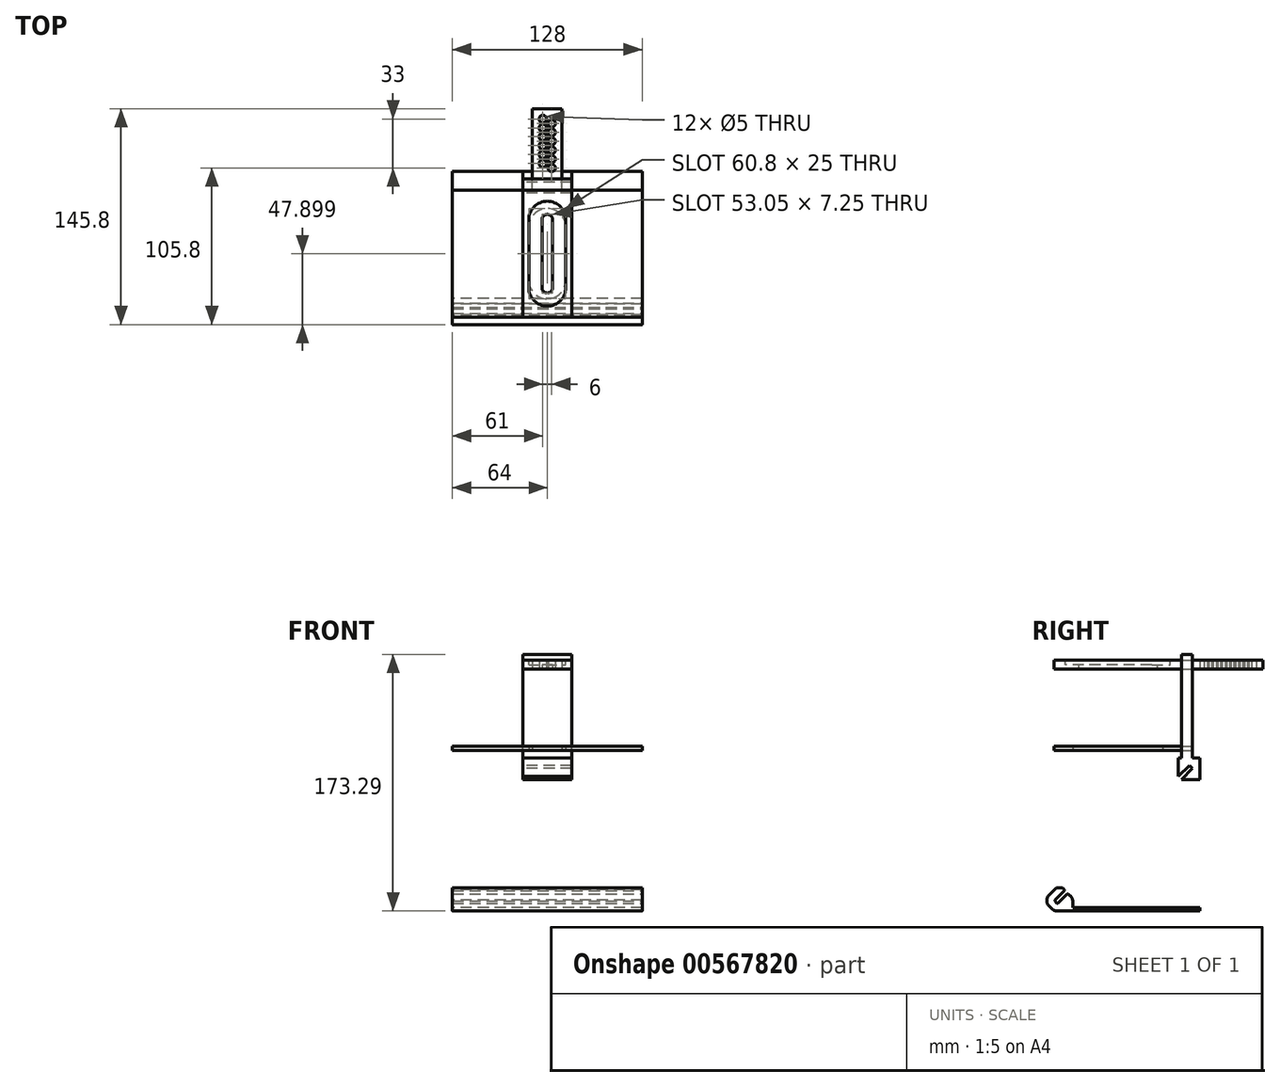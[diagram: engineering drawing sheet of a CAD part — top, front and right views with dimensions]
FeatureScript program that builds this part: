
annotation { "Feature Type Name" : "Feature", "Feature Type Description" : "" }
export const myFeature = defineFeature(function(context is Context, id is Id, definition is map)
    precondition{}
    {
        {
            assignVariable(context, id + "F0", {"name" : "spgBreite", "anyValue" : 128 * mm});
        }
        {
            assignVariable(context, id + "F1", {"name" : "abstDuesen", "anyValue" : 33 * mm});
        }
        {
            var Q0;
            Q0=qCreatedBy(makeId("Right.planeOp"),FACE);
            var sketch = newSketch(context, id + "F2", { "sketchPlane" : qUnion([Q0])});
            skLineSegment(sketch, "E0", {"start": v(0, 0) * mm, "end": v(0, 65) * mm, "construction": true});
            skLineSegment(sketch, "E1", {"start": v(0, 65) * mm, "end": v(-3.25, 65) * mm, "construction": true});
            skLineSegment(sketch, "E2", {"start": v(-3.25, 65) * mm, "end": v(-3.25, 81) * mm, "construction": true});
            skLineSegment(sketch, "E3", {"start": v(-3.25, 81) * mm, "end": v(14.75, 81) * mm, "construction": true});
            skLineSegment(sketch, "E4", {"start": v(14.75, 81) * mm, "end": v(14.75, 0) * mm, "construction": true});
            skLineSegment(sketch, "E5", {"start": v(14.75, 0) * mm, "end": v(0, 0) * mm, "construction": true});
            skLineSegment(sketch, "E6", {"start": v(0, 0) * mm, "end": v(-5, 0) * mm, "construction": true});
            skLineSegment(sketch, "E7", {"start": v(-5, 0) * mm, "end": v(-5, 20) * mm, "construction": true});
            skLineSegment(sketch, "E8", {"start": v(-5, 20) * mm, "end": v(-7.09, 22.09) * mm, "construction": true});
            skLineSegment(sketch, "E9", {"start": v(-7.09, 22.09) * mm, "end": v(-98.3, -69.13) * mm, "construction": true});
            skLineSegment(sketch, "E10", {"start": v(-98.3, -69.13) * mm, "end": v(-96.22, -71.22) * mm, "construction": true});
            skLineSegment(sketch, "E11", {"start": v(-96.22, -71.22) * mm, "end": v(-5, 20) * mm, "construction": true});
            skLineSegment(sketch, "E12", {"start": v(0, 0) * mm, "end": v(0, -150) * mm, "construction": true});
            skLineSegment(sketch, "E13", {"start": v(-98.3, -69.13) * mm, "end": v(-91.23, -62.06) * mm});
            skLineSegment(sketch, "E14", {"start": v(-91.23, -62.06) * mm, "end": v(-94.77, -58.52) * mm});
            skLineSegment(sketch, "E15", {"start": v(-94.77, -58.52) * mm, "end": v(-105.37, -69.13) * mm});
            skLineSegment(sketch, "E16", {"start": v(-105.37, -69.13) * mm, "end": v(-98.3, -76.2) * mm});
            skLineSegment(sketch, "E17", {"start": v(-98.3, -76.2) * mm, "end": v(0, -76.2) * mm});
            skLineSegment(sketch, "E18", {"start": v(0, -76.2) * mm, "end": v(0, -73.7) * mm});
            skLineSegment(sketch, "E19", {"start": v(-85.61, -67.68) * mm, "end": v(-89.15, -64.15) * mm});
            skLineSegment(sketch, "E20", {"start": v(-89.15, -64.15) * mm, "end": v(-96.22, -71.22) * mm});
            skLineSegment(sketch, "E21", {"start": v(-98.3, -69.13) * mm, "end": v(-96.22, -71.22) * mm});
            skLineSegment(sketch, "E22", {"start": v(-85.61, -67.68) * mm, "end": v(-85.61, -73.7) * mm});
            skLineSegment(sketch, "E23", {"start": v(-85.61, -73.7) * mm, "end": v(0, -73.7) * mm});
            skLineSegment(sketch, "E24", {"start": v(-7.09, 22.09) * mm, "end": v(-14.59, 14.59) * mm});
            skLineSegment(sketch, "E25", {"start": v(-12.5, 27.09) * mm, "end": v(-12.5, 97.09) * mm});
            skLineSegment(sketch, "E26", {"start": v(-5, 97.09) * mm, "end": v(-5, 27.09) * mm});
            skLineSegment(sketch, "E27", {"start": v(-5, 27.09) * mm, "end": v(0, 27.09) * mm});
            skLineSegment(sketch, "E28", {"start": v(0, 27.09) * mm, "end": v(0, 12.5) * mm});
            skLineSegment(sketch, "E29", {"start": v(0, 12.5) * mm, "end": v(-12.5, 12.5) * mm});
            skLineSegment(sketch, "E30", {"start": v(-12.5, 12.5) * mm, "end": v(-5, 20) * mm});
            skLineSegment(sketch, "E31", {"start": v(-5, 20) * mm, "end": v(-7.09, 22.09) * mm});
            skLineSegment(sketch, "E32", {"start": v(-98.3, -69.13) * mm, "end": v(-98.3, 130.87) * mm, "construction": true});
            skLineSegment(sketch, "E33", {"start": v(-98.3, -69.13) * mm, "end": v(-98.3, -169.13) * mm, "construction": true});
            skLineSegment(sketch, "E34", {"start": v(-12.5, 27.09) * mm, "end": v(-5, 27.09) * mm, "construction": true});
            skLineSegment(sketch, "E35", {"start": v(-14.5, 27.09) * mm, "end": v(-12.5, 27.09) * mm});
            skLineSegment(sketch, "E36", {"start": v(-14.5, 27.09) * mm, "end": v(-14.59, 14.59) * mm});
            skLineSegment(sketch, "E37", {"start": v(-12.5, 97.09) * mm, "end": v(-5, 97.09) * mm});
            skSolve(sketch);
        }
        {
            var Q0;
            Q0=makeQuery(id+"F2.imprint","IMPRINT",FACE,{"disambiguationData":[TD([[makeQuery(id+"F2.imprint","IMPRINT",EDGE,{"derivedFrom":sQuery(id+"F2.wireOp",EDGE,"E13")}),1.0]])]});
            extrude(context, id + "F3", {"entities" : qUnion([Q0]), "endBound" : BoundingType.SYMMETRIC, "depth" : getVariable(context, 'spgBreite'), "offsetDistance" : 25 * mm});
        }
        {
            var Q0;
            Q0=makeQuery(id+"F3.opExtrude","SWEPT_EDGE",EDGE,{"disambiguationData":[OSD([sQuery(id+"F2.wireOp",EDGE,"E15"),sQuery(id+"F2.wireOp",EDGE,"E16")])]});
            var Q1;
            Q1=makeQuery(id+"F3.opExtrude","SWEPT_EDGE",EDGE,{"disambiguationData":[OSD([sQuery(id+"F2.wireOp",EDGE,"E16"),sQuery(id+"F2.wireOp",EDGE,"E17")])]});
            fillet(context, id + "F4", {"entities" : qUnion([Q0, Q1]), "radius" : 5 * mm, "tangentPropagation" : true, "allowEdgeOverflow" : false});
        }
        {
            var Q0;
            Q0=makeQuery(id+"F3.opExtrude","SWEPT_EDGE",EDGE,{"disambiguationData":[OSD([sQuery(id+"F2.wireOp",EDGE,"E19"),sQuery(id+"F2.wireOp",EDGE,"E22")])]});
            fillet(context, id + "F5", {"entities" : qUnion([Q0]), "radius" : 7.5 * mm, "tangentPropagation" : true, "allowEdgeOverflow" : false});
        }
        {
            var Q0;
            Q0=makeQuery(id+"F3.opExtrude","SWEPT_EDGE",EDGE,{"disambiguationData":[OSD([sQuery(id+"F2.wireOp",EDGE,"E13"),sQuery(id+"F2.wireOp",EDGE,"E21")])]});
            var Q1;
            Q1=makeQuery(id+"F3.opExtrude","SWEPT_EDGE",EDGE,{"disambiguationData":[OSD([sQuery(id+"F2.wireOp",EDGE,"E20"),sQuery(id+"F2.wireOp",EDGE,"E21")])]});
            var Q2;
            Q2=makeQuery(id+"F3.opExtrude","SWEPT_EDGE",EDGE,{"disambiguationData":[OSD([sQuery(id+"F2.wireOp",EDGE,"E19"),sQuery(id+"F2.wireOp",EDGE,"E20")])]});
            var Q3;
            Q3=makeQuery(id+"F3.opExtrude","SWEPT_EDGE",EDGE,{"disambiguationData":[OSD([sQuery(id+"F2.wireOp",EDGE,"E13"),sQuery(id+"F2.wireOp",EDGE,"E14")])]});
            chamfer(context, id + "F6", {"entities" : qUnion([Q0, Q1, Q2, Q3]), "width" : 0.5 * mm, "tangentPropagation" : true});
        }
        {
            var Q0;
            Q0=makeQuery(id+"F3.opExtrude","SWEPT_EDGE",EDGE,{"disambiguationData":[OSD([sQuery(id+"F2.wireOp",EDGE,"E14"),sQuery(id+"F2.wireOp",EDGE,"E15")])]});
            chamfer(context, id + "F7", {"entities" : qUnion([Q0]), "width" : 3 * mm, "tangentPropagation" : true});
        }
        {
            var Q0;
            Q0=makeQuery(id+"F2.imprint","IMPRINT",FACE,{"disambiguationData":[TD([[makeQuery(id+"F2.imprint","IMPRINT",EDGE,{"derivedFrom":sQuery(id+"F2.wireOp",EDGE,"E24")}),-1.0]])]});
            extrude(context, id + "F8", {"entities" : qUnion([Q0]), "endBound" : BoundingType.SYMMETRIC, "depth" : getVariable(context, 'abstDuesen'), "offsetDistance" : 25 * mm});
        }
        {
            var Q0;
            Q0=makeQuery(id+"F8.opExtrude","SWEPT_FACE",FACE,{"disambiguationData":[OSD([sQuery(id+"F2.wireOp",EDGE,"E25")])]});
            var sketch = newSketch(context, id + "F9", { "sketchPlane" : qUnion([Q0])});
            skLineSegment(sketch, "E38", {"start": v(0, 97.09) * mm, "end": v(0, 27.09) * mm, "construction": true});
            skLineSegment(sketch, "E39", {"start": v(-57.12, 35.09) * mm, "end": v(71.94, 35.09) * mm, "construction": true});
            skLineSegment(sketch, "E40", {"start": v(-58.31, 84.59) * mm, "end": v(66.52, 84.59) * mm, "construction": true});
            skLineSegment(sketch, "E41", {"start": v(8, 27.09) * mm, "end": v(8, 97.09) * mm, "construction": true});
            skSolve(sketch);
        }
        {
            var Q0;
            Q0=makeQuery(id+"F8.opExtrude","SWEPT_FACE",FACE,{"disambiguationData":[OSD([sQuery(id+"F2.wireOp",EDGE,"E35")])]});
            cPlane(context, id + "F10", {"entities" : qUnion([Q0]), "cplaneType" : CPlaneType.OFFSET, "offset" : 5 * mm, "width" : 150 * mm, "height" : 150 * mm});
        }
        {
            var Q0;
            Q0=qCreatedBy(id+"F10.planeOp",FACE);
            var sketch = newSketch(context, id + "F11", { "sketchPlane" : qUnion([Q0])});
            skLineSegment(sketch, "E42", {"start": v(-16.5, -12.5) * mm, "end": v(16.5, -12.5) * mm, "construction": true});
            skLineSegment(sketch, "E43", {"start": v(0, 60.07) * mm, "end": v(0, -98.3) * mm, "construction": true});
            skLineSegment(sketch, "E44", {"start": v(0, -98.3) * mm, "end": v(64, -98.3) * mm, "construction": true});
            skLineSegment(sketch, "E45", {"start": v(0, -12.5) * mm, "end": v(-64, -12.5) * mm, "construction": true});
            skLineSegment(sketch, "E46.bottom", {"start": v(64, -98.3) * mm, "end": v(-64, -98.3) * mm});
            skLineSegment(sketch, "E46.top", {"start": v(64, -12.5) * mm, "end": v(-64, -12.5) * mm});
            skLineSegment(sketch, "E46.left", {"start": v(64, -98.3) * mm, "end": v(64, -12.5) * mm});
            skLineSegment(sketch, "E46.right", {"start": v(-64, -98.3) * mm, "end": v(-64, -12.5) * mm});
            skLineSegment(sketch, "E47.bottom", {"start": v(10, -12.5) * mm, "end": v(-10, -12.5) * mm});
            skLineSegment(sketch, "E47.top", {"start": v(10, -5) * mm, "end": v(-10, -5) * mm});
            skLineSegment(sketch, "E47.left", {"start": v(10, -12.5) * mm, "end": v(10, -5) * mm});
            skLineSegment(sketch, "E47.right", {"start": v(-10, -12.5) * mm, "end": v(-10, -5) * mm});
            skCircle(sketch, "E48", {"center": v(0, -37.5) * mm, "radius": 12.5 * mm});
            skCircle(sketch, "E49", {"center": v(0, -73.3) * mm, "radius": 12.5 * mm});
            skLineSegment(sketch, "E50", {"start": v(12.5, -12.5) * mm, "end": v(12.5, -98.3) * mm, "construction": true});
            skLineSegment(sketch, "E51", {"start": v(-12.5, -12.5) * mm, "end": v(-12.5, -98.3) * mm, "construction": true});
            skLineSegment(sketch, "E52", {"start": v(12.5, -73.3) * mm, "end": v(12.5, -37.5) * mm});
            skLineSegment(sketch, "E53", {"start": v(-12.5, -37.5) * mm, "end": v(-12.5, -73.3) * mm});
            skSolve(sketch);
        }
        {
            var Q0;
            Q0 = qSketchRegion(id + "F11", true);
            extrude(context, id + "F12", {"entities" : qUnion([Q0]), "depth" : 3 * mm, "offsetDistance" : 25 * mm});
        }
        {
            var Q0;
            Q0=qCreatedBy(id+"F10.planeOp",FACE);
            cPlane(context, id + "F13", {"entities" : qUnion([Q0]), "cplaneType" : CPlaneType.OFFSET, "offset" : 55 * mm, "width" : 150 * mm, "height" : 150 * mm});
        }
        {
            var Q0;
            Q0=qCreatedBy(id+"F13.planeOp",FACE);
            var sketch = newSketch(context, id + "F14", { "sketchPlane" : qUnion([Q0])});
            skLineSegment(sketch, "E54", {"start": v(0, -12.5) * mm, "end": v(16.5, -12.5) * mm, "construction": true});
            skLineSegment(sketch, "E55", {"start": v(0, -12.5) * mm, "end": v(0, -98.3) * mm, "construction": true});
            skPoint(sketch, "E55.endSnap0", {"position": v(0, -12.5) * mm});
            skLineSegment(sketch, "E56", {"start": v(0, -98.3) * mm, "end": v(16.5, -98.3) * mm, "construction": true});
            skLineSegment(sketch, "E57", {"start": v(0, -12.5) * mm, "end": v(-16.5, -12.5) * mm, "construction": true});
            skLineSegment(sketch, "E58.bottom", {"start": v(16.5, -98.3) * mm, "end": v(-16.5, -98.3) * mm});
            skLineSegment(sketch, "E58.top", {"start": v(16.5, -12.5) * mm, "end": v(-16.5, -12.5) * mm});
            skLineSegment(sketch, "E58.left", {"start": v(16.5, -98.3) * mm, "end": v(16.5, -12.5) * mm});
            skLineSegment(sketch, "E58.right", {"start": v(-16.5, -98.3) * mm, "end": v(-16.5, -12.5) * mm});
            skLineSegment(sketch, "E59.bottom", {"start": v(10, -12.5) * mm, "end": v(-10, -12.5) * mm});
            skLineSegment(sketch, "E59.top", {"start": v(10, 42.5) * mm, "end": v(-10, 42.5) * mm});
            skLineSegment(sketch, "E59.left", {"start": v(10, -12.5) * mm, "end": v(10, 42.5) * mm});
            skLineSegment(sketch, "E59.right", {"start": v(-10, -12.5) * mm, "end": v(-10, 42.5) * mm});
            skLineSegment(sketch, "E60", {"start": v(0, -12.5) * mm, "end": v(0, 42.5) * mm, "construction": true});
            skCircle(sketch, "E61", {"center": v(0, -32.5) * mm, "radius": 3.62 * mm});
            skCircle(sketch, "E62", {"center": v(0, -78.3) * mm, "radius": 3.62 * mm});
            skLineSegment(sketch, "E63", {"start": v(3.62, -32.5) * mm, "end": v(3.62, -78.3) * mm});
            skLineSegment(sketch, "E64", {"start": v(-3.63, -32.5) * mm, "end": v(-3.62, -78.3) * mm});
            skLineSegment(sketch, "E65", {"start": v(-3, -12.5) * mm, "end": v(-3, 42.5) * mm, "construction": true});
            skLineSegment(sketch, "E66", {"start": v(3, 42.5) * mm, "end": v(3, -12.5) * mm, "construction": true});
            skCircle(sketch, "E67", {"center": v(-3, 5.5) * mm, "radius": 2.5 * mm});
            skCircle(sketch, "E68", {"center": v(3, 2.5) * mm, "radius": 2.5 * mm});
            skLineSegment(sketch, "E69", {"start": v(0, 34.58) * mm, "end": v(-3, 34.58) * mm});
            skLineSegment(sketch, "E70", {"start": v(0, 34.58) * mm, "end": v(3, 34.58) * mm});
            skCircle(sketch, "E71.1.0.0", {"center": v(-3, 11.5) * mm, "radius": 2.5 * mm});
            skCircle(sketch, "E71.2.0.0", {"center": v(-3, 17.5) * mm, "radius": 2.5 * mm});
            skLineSegment(sketch, "E71.direction1", {"start": v(-3, 5.5) * mm, "end": v(-3, 11.5) * mm, "construction": true});
            skCircle(sketch, "E72.0.3.0", {"center": v(-3, 23.5) * mm, "radius": 2.5 * mm});
            skCircle(sketch, "E72.0.4.0", {"center": v(-3, 29.5) * mm, "radius": 2.5 * mm});
            skCircle(sketch, "E72.0.5.0", {"center": v(-3, 35.5) * mm, "radius": 2.5 * mm});
            skCircle(sketch, "E73.1.0.0", {"center": v(3, 8.5) * mm, "radius": 2.5 * mm});
            skCircle(sketch, "E73.2.0.0", {"center": v(3, 14.5) * mm, "radius": 2.5 * mm});
            skLineSegment(sketch, "E73.direction1", {"start": v(3, 2.5) * mm, "end": v(3, 8.5) * mm, "construction": true});
            skCircle(sketch, "E74.0.3.0", {"center": v(3, 20.5) * mm, "radius": 2.5 * mm});
            skCircle(sketch, "E74.0.4.0", {"center": v(3, 26.5) * mm, "radius": 2.5 * mm});
            skCircle(sketch, "E74.0.5.0", {"center": v(3, 32.5) * mm, "radius": 2.5 * mm});
            skSolve(sketch);
        }
        {
            var Q0;
            Q0 = qSketchRegion(id + "F14", true);
            extrude(context, id + "F15", {"entities" : qUnion([Q0]), "depth" : 6 * mm, "offsetDistance" : 25 * mm});
        }
        {
            var Q0;
            Q0=makeQuery(id+"F15.opExtrude","CAP_FACE",FACE,{"disambiguationData":[OSD([sQuery(id+"F14.wireOp",EDGE,"E58.bottom"),sQuery(id+"F14.wireOp",EDGE,"E58.top"),sQuery(id+"F14.wireOp",EDGE,"E58.left"),sQuery(id+"F14.wireOp",EDGE,"E58.right"),sQuery(id+"F14.wireOp",EDGE,"E59.top"),sQuery(id+"F14.wireOp",EDGE,"E59.left"),sQuery(id+"F14.wireOp",EDGE,"E59.right"),sQuery(id+"F14.wireOp",EDGE,"E61"),sQuery(id+"F14.wireOp",EDGE,"E62"),sQuery(id+"F14.wireOp",EDGE,"E63"),sQuery(id+"F14.wireOp",EDGE,"E64")])],"isStart":false});
            var sketch = newSketch(context, id + "F16", { "sketchPlane" : qUnion([Q0])});
            skLineSegment(sketch, "E75", {"start": v(0, -98.3) * mm, "end": v(0, -12.5) * mm, "construction": true});
            skLineSegment(sketch, "E76", {"start": v(3.62, -32.5) * mm, "end": v(-3.63, -32.5) * mm, "construction": true});
            skLineSegment(sketch, "E77", {"start": v(3.62, -78.3) * mm, "end": v(-3.62, -78.3) * mm, "construction": true});
            skCircle(sketch, "E78", {"center": v(0, -32.5) * mm, "radius": 12.5 * mm});
            skCircle(sketch, "E79", {"center": v(0, -78.3) * mm, "radius": 12.5 * mm});
            skLineSegment(sketch, "E80", {"start": v(-12.5, -32.5) * mm, "end": v(-12.5, -78.3) * mm});
            skLineSegment(sketch, "E81", {"start": v(12.5, -32.5) * mm, "end": v(12.5, -78.3) * mm});
            skSolve(sketch);
        }
        {
            var Q0;
            Q0 = qSketchRegion(id + "F16", true);
            extrude(context, id + "F17", {"entities" : qUnion([Q0]), "operationType" : NewBodyOperationType.REMOVE, "oppositeDirection" : true, "depth" : 3 * mm, "offsetDistance" : 25 * mm});
        }
    });
